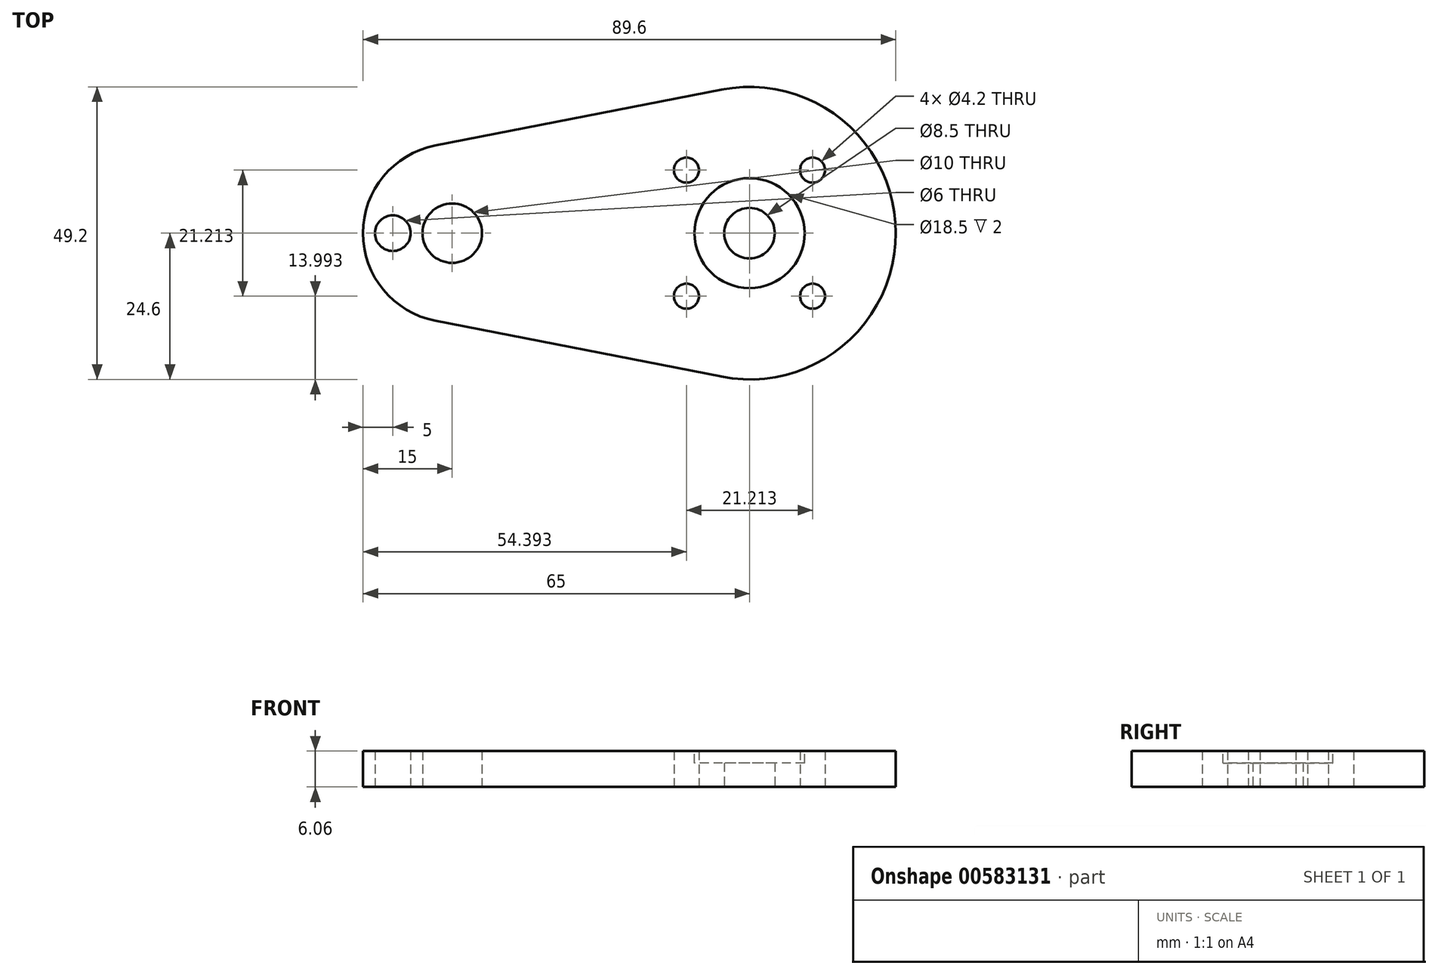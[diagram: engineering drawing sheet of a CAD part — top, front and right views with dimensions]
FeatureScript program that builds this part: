
annotation { "Feature Type Name" : "Feature", "Feature Type Description" : "" }
export const myFeature = defineFeature(function(context is Context, id is Id, definition is map)
    precondition{}
    {
        {
            var Q0;
            Q0=qCreatedBy(makeId("Top.planeOp"),FACE);
            var sketch = newSketch(context, id + "F0", { "sketchPlane" : qUnion([Q0])});
            skCircle(sketch, "E0", {"center": v(0, 0) * mm, "radius": 15 * mm, "construction": true});
            skCircle(sketch, "E1", {"center": v(0, 0) * mm, "radius": 4.25 * mm});
            skLineSegment(sketch, "E2", {"start": v(0, 0) * mm, "end": v(-10.6, 10.6) * mm, "construction": true});
            skCircle(sketch, "E3", {"center": v(-10.6, 10.6) * mm, "radius": 2.1 * mm});
            skCircle(sketch, "E4.1.0", {"center": v(-10.6, -10.6) * mm, "radius": 2.1 * mm});
            skCircle(sketch, "E4.2.0", {"center": v(10.6, -10.6) * mm, "radius": 2.1 * mm});
            skCircle(sketch, "E4.3.0", {"center": v(10.6, 10.6) * mm, "radius": 2.1 * mm});
            skLineSegment(sketch, "E5", {"start": v(0, 0) * mm, "end": v(10.6, 10.6) * mm, "construction": true});
            skLineSegment(sketch, "E6", {"start": v(0, 0) * mm, "end": v(10.6, -10.6) * mm, "construction": true});
            skLineSegment(sketch, "E7", {"start": v(0, 0) * mm, "end": v(-10.6, -10.6) * mm, "construction": true});
            skCircle(sketch, "E8", {"center": v(0, 0) * mm, "radius": 24.6 * mm});
            skCircle(sketch, "E9", {"center": v(-50, 0) * mm, "radius": 15 * mm});
            skLineSegment(sketch, "E10", {"start": v(-4.72, 24.14) * mm, "end": v(-52.88, 14.72) * mm});
            skLineSegment(sketch, "E11", {"start": v(-52.88, -14.72) * mm, "end": v(-4.72, -24.14) * mm});
            skCircle(sketch, "E12", {"center": v(-50, 0) * mm, "radius": 5 * mm});
            skCircle(sketch, "E13", {"center": v(-60, 0) * mm, "radius": 3 * mm});
            skSolve(sketch);
        }
        {
            var Q0;
            Q0 = qSketchRegion(id + "F0", true);
            extrude(context, id + "F1", {"entities" : qUnion([Q0]), "endBound" : BoundingType.SYMMETRIC, "depth" : 6.05 * mm, "offsetDistance" : 25 * mm});
        }
        {
            var Q0;
            Q0=makeQuery(id+"F1.opExtrude","CAP_FACE",FACE,{"disambiguationData":[OSD([sQuery(id+"F0.wireOp",EDGE,"E1"),sQuery(id+"F0.wireOp",EDGE,"E3"),sQuery(id+"F0.wireOp",EDGE,"E4.1.0"),sQuery(id+"F0.wireOp",EDGE,"E4.2.0"),sQuery(id+"F0.wireOp",EDGE,"E4.3.0"),sQuery(id+"F0.wireOp",EDGE,"E8"),sQuery(id+"F0.wireOp",EDGE,"E9"),sQuery(id+"F0.wireOp",EDGE,"E10"),sQuery(id+"F0.wireOp",EDGE,"E11"),sQuery(id+"F0.wireOp",EDGE,"E12"),sQuery(id+"F0.wireOp",EDGE,"E13")])],"isStart":false});
            var sketch = newSketch(context, id + "F2", { "sketchPlane" : qUnion([Q0])});
            skCircle(sketch, "E14", {"center": v(0, 0) * mm, "radius": 9.25 * mm});
            skSolve(sketch);
        }
        {
            var Q0;
            Q0 = qSketchRegion(id + "F2", true);
            extrude(context, id + "F3", {"entities" : qUnion([Q0]), "operationType" : NewBodyOperationType.REMOVE, "oppositeDirection" : true, "depth" : 2 * mm, "offsetDistance" : 25 * mm});
        }
    });
